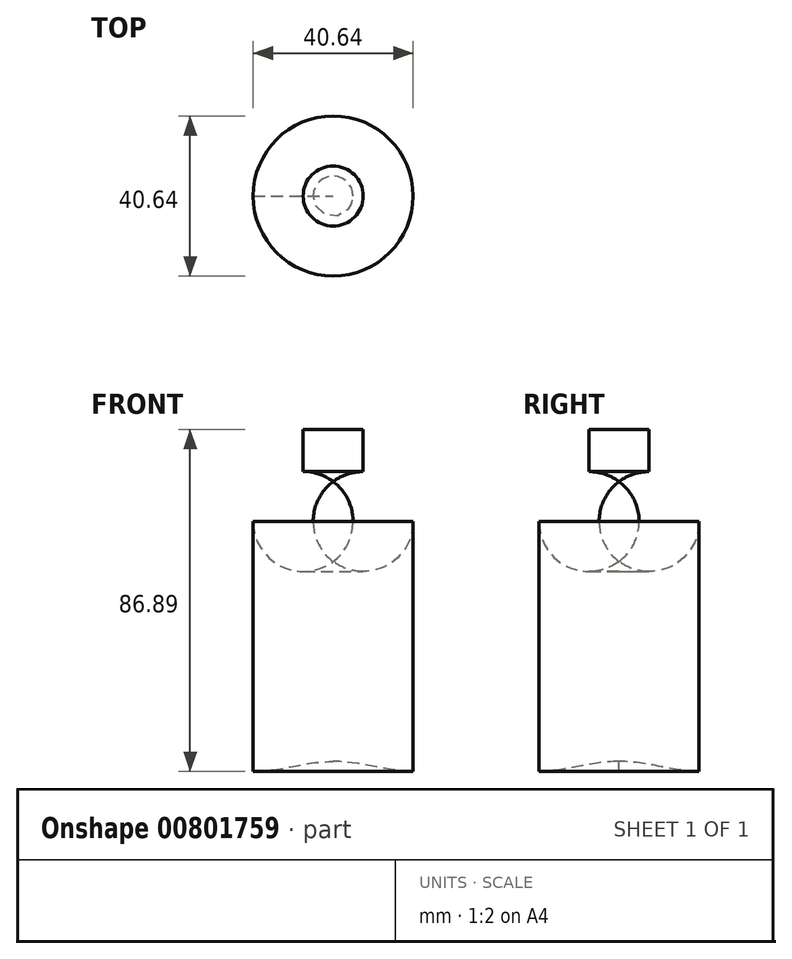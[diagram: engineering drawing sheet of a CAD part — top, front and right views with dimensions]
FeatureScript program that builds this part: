
annotation { "Feature Type Name" : "Feature", "Feature Type Description" : "" }
export const myFeature = defineFeature(function(context is Context, id is Id, definition is map)
    precondition{}
    {
        {
            var Q0;
            Q0=qCreatedBy(makeId("Front.planeOp"),FACE);
            var sketch = newSketch(context, id + "F0", { "sketchPlane" : qUnion([Q0])});
            skLineSegment(sketch, "E0", {"start": v(0, -20.81) * mm, "end": v(0, 52.85) * mm});
            skLineSegment(sketch, "E1", {"start": v(-20.32, -23.35) * mm, "end": v(-20.32, 40.15) * mm});
            skLineSegment(sketch, "E2", {"start": v(-7.62, 52.85) * mm, "end": v(0, 52.85) * mm});
            skPoint(sketch, "E3.visualSharp", {"position": v(-20.32, 52.85) * mm});
            skArc(sketch, "E3.filletArc", {"start": v(-7.62, 52.85) * mm, "mid": v(-16.6, 49.13) * mm, "end": v(-20.32, 40.15) * mm});
            skFitSpline(sketch, "E4", {"points": [v(-20.32, -23.35) * mm, v(0, -20.81) * mm], "startDerivative": vector(26.17, 1.03) * mm, "endDerivative": vector(23.55, 0.15) * mm});
            skLineSegment(sketch, "E5.top", {"start": v(-7.62, 63.54) * mm, "end": v(0, 63.54) * mm});
            skLineSegment(sketch, "E5.left", {"start": v(-7.62, 52.85) * mm, "end": v(-7.62, 63.54) * mm});
            skLineSegment(sketch, "E5.right", {"start": v(0, 52.85) * mm, "end": v(0, 63.54) * mm});
            skSolve(sketch);
        }
        {
            var Q0;
            Q0 = qSketchRegion(id + "F0", true);
            var Q1;
            Q1=sQuery(id+"F0.wireOp",EDGE,"E0");
            revolve(context, id + "F1", {"surfaceOperationType" : NewSurfaceOperationType.NEW, "entities" : qUnion([Q0]), "axis" : qUnion([Q1]), "revolveType" : RevolveType.FULL});
        }
    });
